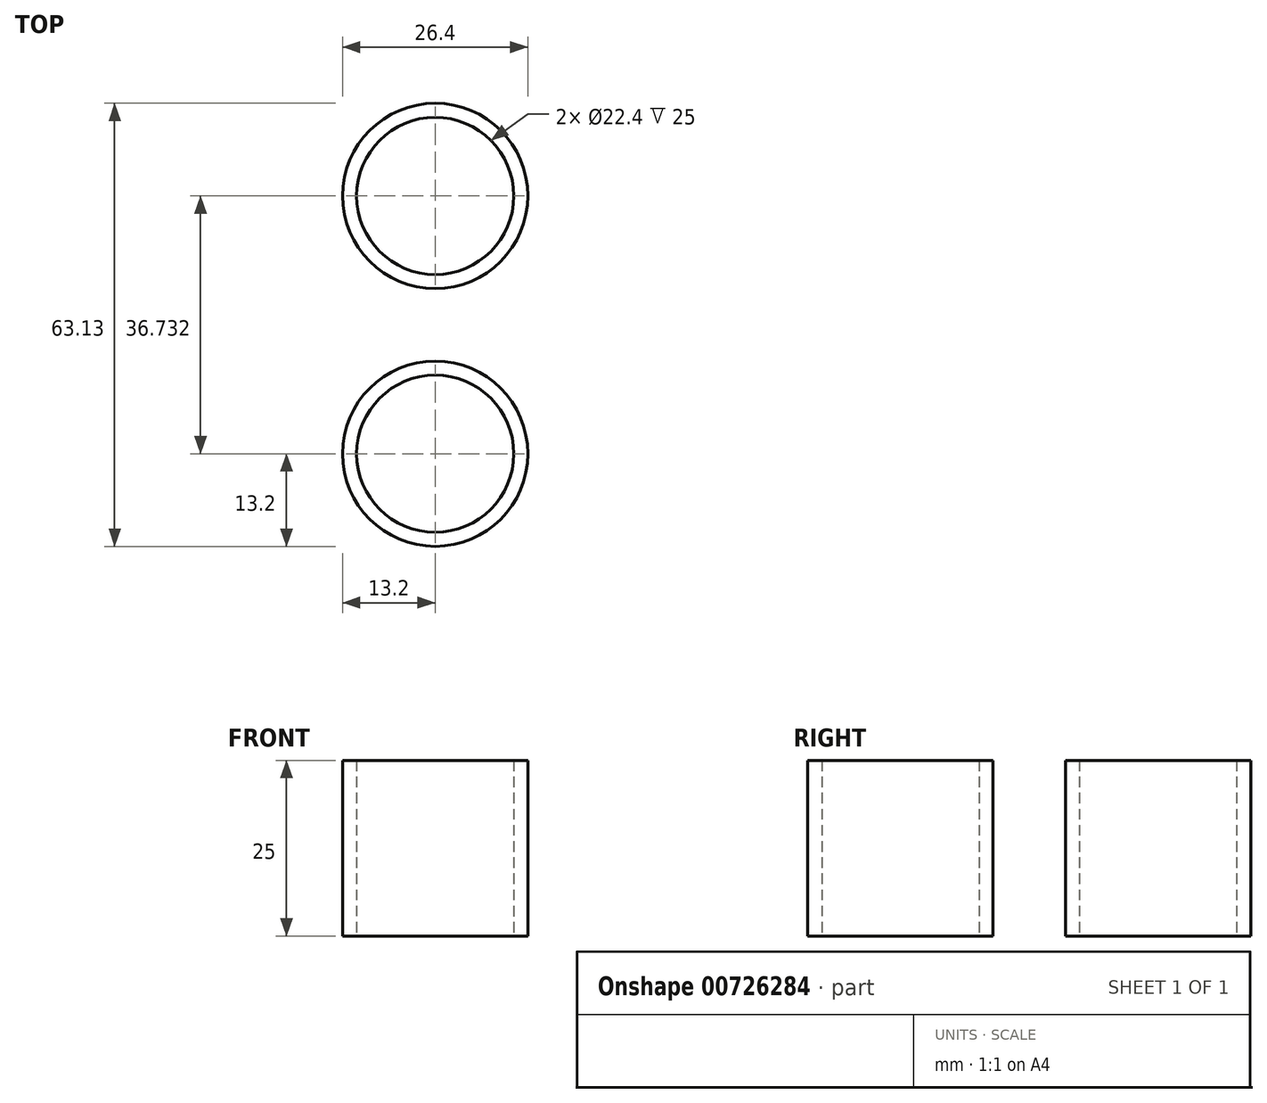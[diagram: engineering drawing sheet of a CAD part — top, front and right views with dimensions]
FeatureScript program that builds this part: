
annotation { "Feature Type Name" : "Feature", "Feature Type Description" : "" }
export const myFeature = defineFeature(function(context is Context, id is Id, definition is map)
    precondition{}
    {
        {
            var Q0;
            Q0=qCreatedBy(makeId("Top.planeOp"),FACE);
            var sketch = newSketch(context, id + "F0", { "sketchPlane" : qUnion([Q0])});
            skCircle(sketch, "E0", {"center": v(0, 0) * mm, "radius": 11.2 * mm});
            skCircle(sketch, "E1", {"center": v(0, 0) * mm, "radius": 13.2 * mm});
            skCircle(sketch, "E2", {"center": v(0, 36.73) * mm, "radius": 11.2 * mm});
            skCircle(sketch, "E3", {"center": v(0, 36.73) * mm, "radius": 13.2 * mm});
            skSolve(sketch);
        }
        {
            var Q0;
            Q0 = qSketchRegion(id + "F0", true);
            extrude(context, id + "F1", {"entities" : qUnion([Q0]), "depth" : 25 * mm, "offsetDistance" : 25 * mm});
        }
    });
